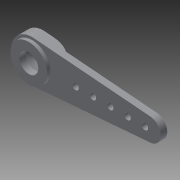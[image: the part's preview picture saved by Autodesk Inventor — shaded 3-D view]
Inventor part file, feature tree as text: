
AUTODESK INVENTOR PART (.ipt)
format: ipt  version: 2015 SP2 (Build 190223200, 223)  size: 147,968 bytes
history: native  units: mm
features: sketch x7, extrude x4, hole x3, fillet x1
ambient origin geometry x8: Origin, YZ Plane, XZ Plane, XY Plane, X Axis, Y Axis, Z Axis, Center Point
bodies: Solid1 (feature_tree)
feature tree (15):
  extrude  "Extrusion1"  Depth=11.314mm
  extrude  "Extrusion2"  Depth=3.0mm
  fillet  "Fillet1"  Radius=36.0mm
  sketch  "Sketch4"  dims[d5=7.0mm d6=2.0mm d7=0.0mm]
  extrude  "Extrusion3"  Depth=2.0mm TaperAngle=0.0deg
  extrude  "Extrusion4"  Depth=10.0mm
  hole  "Hole1"  [1 undecoded]
  hole  "Hole2"  [1 undecoded]
  hole  "Hole4"  [1 undecoded]
  sketch  "Sketch1"  dims[d0=12.9mm d1=11.314mm]
  sketch  "Sketch2"  dims[d2=5.7mm d3=3.0mm d4=36.0mm]
  sketch  "Sketch5"  dims[d8=1.5mm d9=0.0mm d10=10.0mm]
  sketch  "Sketch6"  dims[d11=5.8mm d12=3.0mm]
  sketch  "Sketch7"  dims[d13=0.5mm d14=0.0mm d15=3.0mm d16=0.0mm]
  sketch  "Sketch9"  dims[d17=5.8mm d18=0.5mm d19=0.0mm d20=3.0mm d21=6.0mm d22=4.0mm d23=2.0mm d24=90.0deg d25=8.0mm d26=20.594885mm d27=5.8mm d28=5.8mm d29=6.0mm d30=4.0mm d31=2.0mm d32=90.0deg d33=2.0mm d34=20.594885mm d47=2.0mm d48=6.0mm d49=4.0mm d50=2.0mm d51=90.0deg d52=1.0mm d53=20.594885mm]
note: 3 required parameter values undecoded (feature->parameter linkage not recoverable at this tier; creation-order binding heuristic only, values carry confidence <= 0.55)
